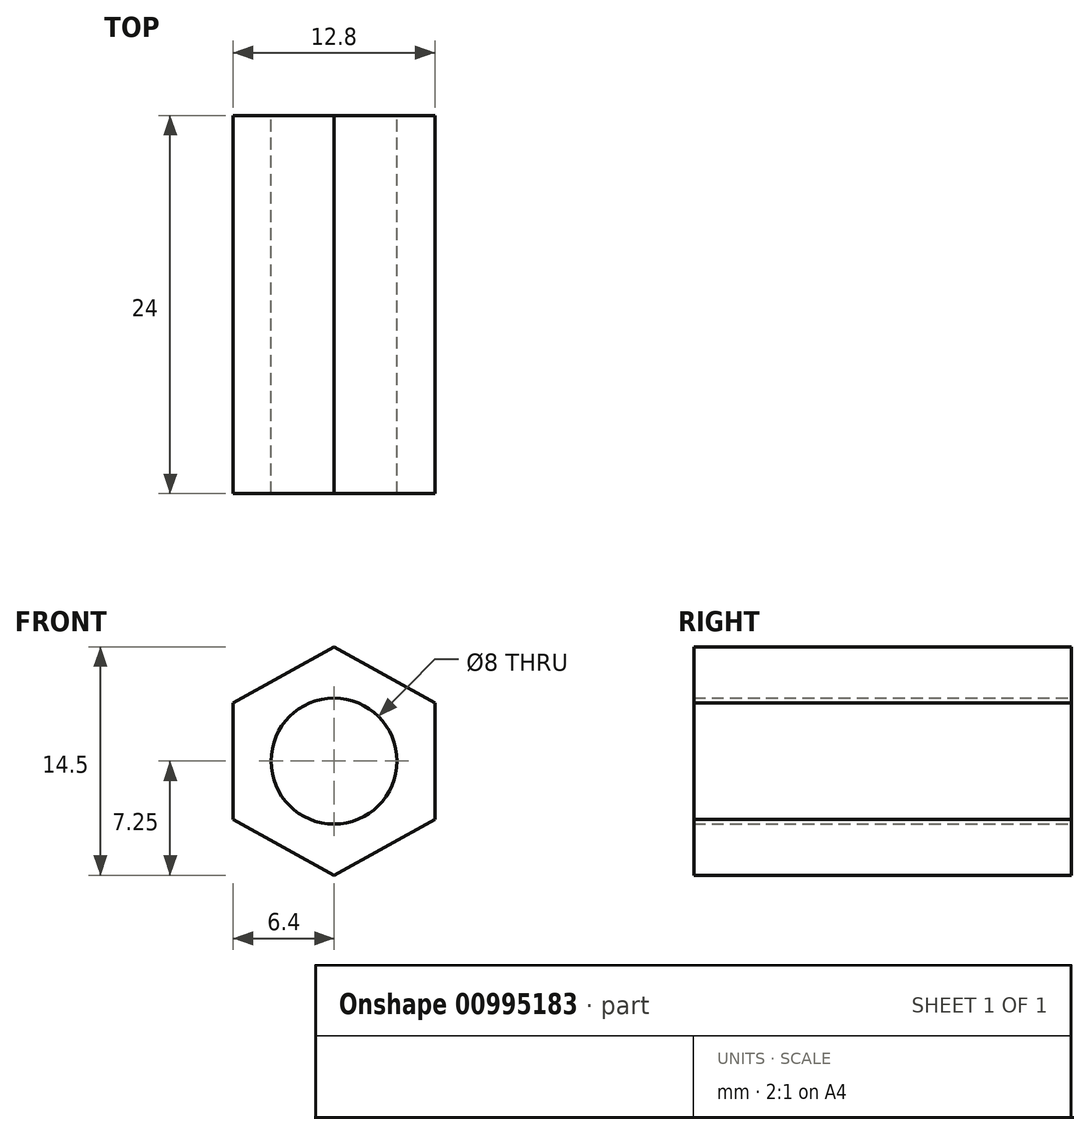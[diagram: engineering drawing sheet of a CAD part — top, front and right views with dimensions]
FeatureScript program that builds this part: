
annotation { "Feature Type Name" : "Feature", "Feature Type Description" : "" }
export const myFeature = defineFeature(function(context is Context, id is Id, definition is map)
    precondition{}
    {
        {
            var Q0;
            Q0=qCreatedBy(makeId("Front.planeOp"),FACE);
            var sketch = newSketch(context, id + "F0", { "sketchPlane" : qUnion([Q0])});
            skPoint(sketch, "E0.middle", {"position": v(0, 0) * mm});
            skLineSegment(sketch, "E1", {"start": v(-6.4, 3.7) * mm, "end": v(0, 7.25) * mm});
            skLineSegment(sketch, "E2", {"start": v(0, 7.25) * mm, "end": v(6.4, 3.7) * mm});
            skLineSegment(sketch, "E3", {"start": v(6.4, 3.7) * mm, "end": v(6.4, -3.7) * mm});
            skLineSegment(sketch, "E4", {"start": v(6.4, -3.7) * mm, "end": v(0, -7.25) * mm});
            skLineSegment(sketch, "E5", {"start": v(0, -7.25) * mm, "end": v(-6.4, -3.7) * mm});
            skLineSegment(sketch, "E6", {"start": v(-6.4, -3.7) * mm, "end": v(-6.4, 3.7) * mm});
            skSolve(sketch);
        }
        {
            var Q0;
            Q0=makeQuery(id+"F0.imprint","IMPRINT",FACE,{"disambiguationData":[TD([[makeQuery(id+"F0.imprint","IMPRINT",EDGE,{"derivedFrom":sQuery(id+"F0.wireOp",EDGE,"E2")}),-1.0]])]});
            extrude(context, id + "F1", {"entities" : qUnion([Q0]), "depth" : 24 * mm, "offsetDistance" : 25 * mm, "symmetric" : true});
        }
        {
            var Q0;
            Q0=makeQuery(id+"F1.opExtrude","CAP_FACE",FACE,{"disambiguationData":[OSD([sQuery(id+"F0.wireOp",EDGE,"E2"),sQuery(id+"F0.wireOp",EDGE,"E3"),sQuery(id+"F0.wireOp",EDGE,"E4"),sQuery(id+"F0.wireOp",EDGE,"E5"),sQuery(id+"F0.wireOp",EDGE,"E6"),sQuery(id+"F0.wireOp",EDGE,"E1")])],"isStart":false});
            var sketch = newSketch(context, id + "F2", { "sketchPlane" : qUnion([Q0])});
            skPoint(sketch, "E7", {"position": v(0, 0) * mm});
            skSolve(sketch);
        }
        {
            var Q0;
            Q0=sQuery(id+"F2.wireOp",VERTEX,"E7");
            var Q1;
            Q1=makeQuery(id+"F1.opExtrude","SWEPT_BODY",BODY,{"disambiguationData":[OSD([sQuery(id+"F0.wireOp",EDGE,"E2"),sQuery(id+"F0.wireOp",EDGE,"E3"),sQuery(id+"F0.wireOp",EDGE,"E4"),sQuery(id+"F0.wireOp",EDGE,"E5"),sQuery(id+"F0.wireOp",EDGE,"E6"),sQuery(id+"F0.wireOp",EDGE,"E1")])]});
            hole(context, id + "F3", {"style" : HoleStyle.SIMPLE, "endStyle" : HoleEndStyle.THROUGH, "holeDiameter" : 8 * mm, "majorDiameter" : 5 * mm, "isTappedThrough" : true, "tappedDepth" : 12 * mm, "tapClearance" : 3, "locations" : qUnion([Q0]), "scope" : qUnion([Q1]), "startStyle" : HoleStartStyle.PART});
        }
    });
